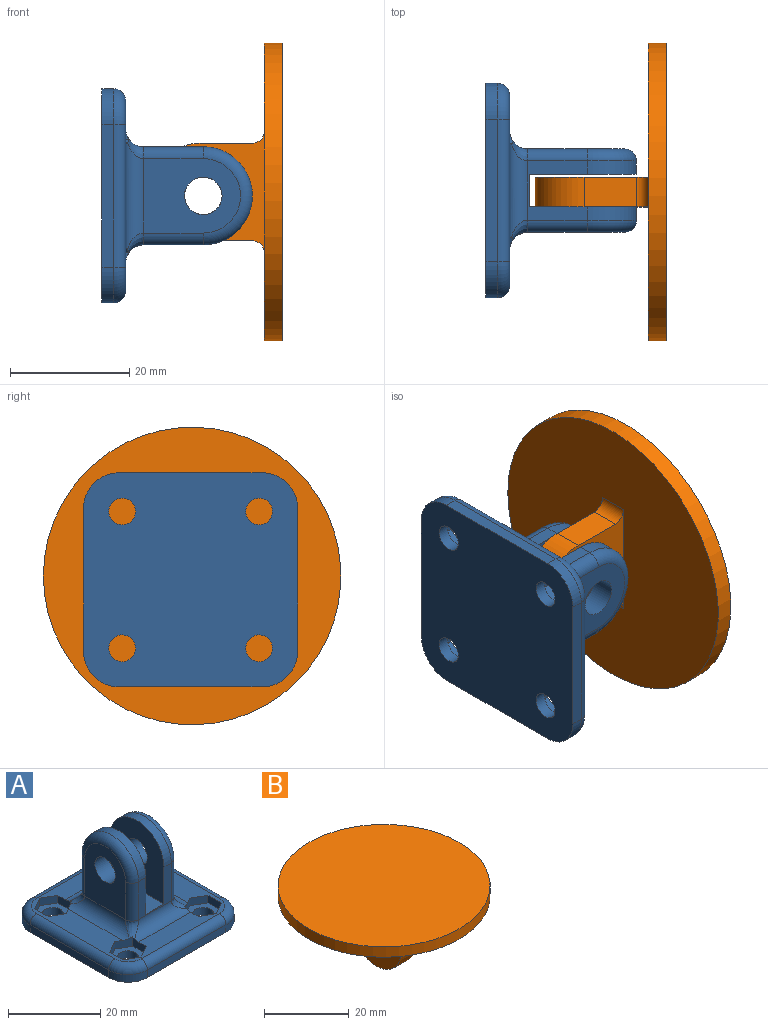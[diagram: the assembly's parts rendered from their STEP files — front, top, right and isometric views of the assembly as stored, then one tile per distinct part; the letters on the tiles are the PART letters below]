
ASSEMBLY  parts=2 mates=1
PART A: 75 faces, bbox 37x37x26 mm
  f0: plane 16.3x12.5mm, normal (1,0,0), area 155.8mm2, adj f51,f55,f71,f72,f73
  f1: plane 16.3x12.5mm, normal (-1,0,0), area 155.8mm2, adj f48,f53,f66,f67,f68
  f2: plane 18x16.5mm, normal (-1,0,0), area 236.6mm2, adj f4,f47,f52,f55,f56
  f3: plane 18x16.5mm, normal (1,0,0), area 236.6mm2, adj f4,f47,f52,f53,f54
  f4: plane 10.05x10mm, normal (0,-1,0), area 46.9mm2, adj f2,f3,f49,f52,f54,f56,f66,f71
  f5: plane 3.6x2.54mm, normal (0.5,0.87,0), area 8.7mm2, adj f6,f36,f37,f46,f51,f74
  f6: plane 4.15x2.54mm, normal (1,0,0), area 8.5mm2, adj f5,f7,f37,f46,f50,f74
  f7: plane 3.55x2.05mm, normal (0.5,-0.87,0), area 8.2mm2, adj f6,f8,f37,f46
  f8: plane 3.55x2.05mm, normal (-0.5,-0.87,0), area 8.2mm2, adj f7,f9,f37,f46
  f9: plane 4.1x2mm, normal (-1,0,0), area 8.2mm2, adj f8,f36,f37,f46
  f10: plane 3.55x2.05mm, normal (0.5,0.87,0), area 8.2mm2, adj f11,f32,f37,f42
  f11: plane 4.15x2.54mm, normal (1,0,0), area 8.5mm2, adj f10,f12,f37,f42,f49,f70
  f12: plane 3.6x2.54mm, normal (0.5,-0.87,0), area 8.7mm2, adj f11,f13,f37,f42,f51,f70
  f13: plane 3.55x2.05mm, normal (-0.5,-0.87,0), area 8.2mm2, adj f12,f14,f37,f42
  f14: plane 4.1x2mm, normal (-1,0,0), area 8.2mm2, adj f13,f32,f37,f42
  f15: plane 3.55x2.05mm, normal (-0.5,-0.87,0), area 8.2mm2, adj f16,f33,f37,f44
  f16: plane 4.15x2.54mm, normal (-1,0,0), area 8.5mm2, adj f15,f17,f37,f44,f50,f69
  f17: plane 3.6x2.54mm, normal (-0.5,0.87,0), area 8.7mm2, adj f16,f18,f37,f44,f48,f69
  f18: plane 3.55x2.05mm, normal (0.5,0.87,0), area 8.2mm2, adj f17,f19,f37,f44
  f19: plane 4.1x2mm, normal (1,0,0), area 8.2mm2, adj f18,f33,f37,f44
  f20: plane 3.6x2.54mm, normal (-0.5,-0.87,0), area 8.7mm2, adj f21,f34,f37,f40,f48,f65
  f21: plane 4.15x2.54mm, normal (-1,0,0), area 8.5mm2, adj f20,f22,f37,f40,f49,f65
  f22: plane 3.55x2.05mm, normal (-0.5,0.87,0), area 8.2mm2, adj f21,f23,f37,f40
  f23: plane 3.55x2.05mm, normal (0.5,0.87,0), area 8.2mm2, adj f22,f24,f37,f40
  f24: plane 4.1x2mm, normal (1,0,0), area 8.2mm2, adj f23,f34,f37,f40
  f25: plane 24x2mm, normal (0,-1,0), area 48mm2, adj f26,f35,f38,f61
  f26: cylinder r=6mm len=6mm, axis (0,0,-1), area 18.8mm2, adj f25,f27,f38,f59
  f27: plane 24x2mm, normal (1,0,0), area 48mm2, adj f26,f28,f38,f57
  f28: cylinder r=6mm len=6mm, axis (0,0,-1), area 18.8mm2, adj f27,f29,f38,f58
  f29: plane 24x2mm, normal (0,1,0), area 48mm2, adj f28,f30,f38,f60
  f30: cylinder r=6mm len=6mm, axis (0,0,-1), area 18.8mm2, adj f29,f31,f38,f62
  f31: plane 24x2mm, normal (-1,0,0), area 48mm2, adj f30,f35,f38,f64
  f32: plane 3.55x2.05mm, normal (-0.5,0.87,0), area 8.2mm2, adj f10,f14,f37,f42
  f33: plane 3.55x2.05mm, normal (0.5,-0.87,0), area 8.2mm2, adj f15,f19,f37,f44
  f34: plane 3.55x2.05mm, normal (0.5,-0.87,0), area 8.2mm2, adj f20,f24,f37,f40
  f35: cylinder r=6mm len=6mm, axis (0,0,-1), area 18.8mm2, adj f25,f31,f38,f63
  f36: plane 3.55x2.05mm, normal (-0.5,0.87,0), area 8.2mm2, adj f5,f9,f37,f46
  f37: plane 32x32mm, normal (0,0,1), area 405.2mm2, adj f5,f6,f7,f8,f9,f10,f11,f12
  f38: plane 36x36mm, normal (0,0,-1), area 1201.5mm2, adj f25,f26,f27,f28,f29,f30,f31,f35
  f39: cylinder r=2.25mm len=4.5mm, axis (0,0,-1), area 28.3mm2, adj f38,f40
  f40: plane 8.2x7.1mm, normal (0,0,1), area 27.8mm2, adj f20,f21,f22,f23,f24,f34,f39
  f41: cylinder r=2.25mm len=4.5mm, axis (0,0,-1), area 28.3mm2, adj f38,f42
  f42: plane 8.2x7.1mm, normal (0,0,1), area 27.8mm2, adj f10,f11,f12,f13,f14,f32,f41
  f43: cylinder r=2.25mm len=4.5mm, axis (0,0,-1), area 28.3mm2, adj f38,f44
  f44: plane 8.2x7.1mm, normal (0,0,1), area 27.8mm2, adj f15,f16,f17,f18,f19,f33,f43
  f45: cylinder r=2.25mm len=4.5mm, axis (0,0,-1), area 28.3mm2, adj f38,f46
  f46: plane 8.2x7.1mm, normal (0,0,1), area 27.8mm2, adj f5,f6,f7,f8,f9,f36,f45
  f47: plane 10.05x10mm, normal (0,1,0), area 46.9mm2, adj f2,f3,f50,f52,f54,f56,f68,f73
  f48: cylinder r=3mm len=18.07mm, axis (0,1,0), area 74.8mm2, adj f1,f17,f20,f37,f65,f69
  f49: cylinder r=3mm len=15.9mm, axis (-1,0,0), area 61.7mm2, adj f4,f11,f21,f37,f65,f70
  f50: cylinder r=3mm len=15.9mm, axis (1,0,0), area 61.7mm2, adj f6,f16,f37,f47,f69,f74
  f51: cylinder r=3mm len=18.07mm, axis (0,-1,0), area 74.8mm2, adj f0,f5,f12,f37,f70,f74
  f52: plane 16.5x5.5mm, normal (0,0,1), area 90.7mm2, adj f2,f3,f4,f47
  f53: cylinder r=3.15mm len=6.3mm, axis (1,0,0), area 84.1mm2, adj f1,f3
  f54: cylinder r=8.25mm len=16.5mm, axis (1,0,0), area 58.3mm2, adj f3,f4,f47,f67
  f55: cylinder r=3.15mm len=6.3mm, axis (1,0,0), area 84.1mm2, adj f0,f2
  f56: cylinder r=8.25mm len=16.5mm, axis (1,0,0), area 58.3mm2, adj f2,f4,f47,f72
  f57: cylinder r=2mm len=24mm, axis (0,-1,0), area 75.4mm2, adj f27,f37,f58,f59
  f58: torus R=4mm, axis (0,0,1), area 26mm2, adj f28,f37,f57,f60
  f59: torus R=4mm, axis (0,0,1), area 26mm2, adj f26,f37,f57,f61
  f60: cylinder r=2mm len=24mm, axis (1,0,0), area 75.4mm2, adj f29,f37,f58,f62
  f61: cylinder r=2mm len=24mm, axis (-1,0,0), area 75.4mm2, adj f25,f37,f59,f63
  f62: torus R=4mm, axis (0,0,1), area 26mm2, adj f30,f37,f60,f64
  f63: torus R=4mm, axis (0,0,1), area 26mm2, adj f35,f37,f61,f64
  f64: cylinder r=2mm len=24mm, axis (0,1,0), area 75.4mm2, adj f31,f37,f62,f63
  f65: bspline ~3.94x3.94mm, area 9.3mm2, adj f20,f21,f48,f49,f66
  f66: cylinder r=2mm len=10.05mm, axis (0,0,1), area 31.6mm2, adj f1,f4,f65,f67
  f67: torus R=6.25mm, axis (1,0,0), area 74.3mm2, adj f1,f54,f66,f68
  f68: cylinder r=2mm len=10.05mm, axis (0,0,-1), area 31.6mm2, adj f1,f47,f67,f69
  f69: bspline ~3.94x3.94mm, area 9.3mm2, adj f16,f17,f48,f50,f68
  f70: bspline ~3.94x3.94mm, area 9.3mm2, adj f11,f12,f49,f51,f71
  f71: cylinder r=2mm len=10.05mm, axis (0,0,-1), area 31.6mm2, adj f0,f4,f70,f72
  f72: torus R=6.25mm, axis (1,0,0), area 74.3mm2, adj f0,f56,f71,f73
  f73: cylinder r=2mm len=10.05mm, axis (0,0,1), area 31.6mm2, adj f0,f47,f72,f74
  f74: bspline ~3.94x3.94mm, area 9.3mm2, adj f5,f6,f50,f51,f73
PART B: 11 faces, bbox 50x50x22 mm
  f0: plane 50x50mm, normal (0,0,-1), area 1861.5mm2, adj f1,f3,f5,f9,f10
  f1: cylinder r=25mm len=50mm, axis (0,0,-1), area 471.2mm2, adj f0,f2
  f2: plane 50x50mm, normal (0,0,1), area 1963.5mm2, adj f1
  f3: plane 20.4x19mm, normal (1,0,0), area 251.3mm2, adj f0,f4,f6,f7,f8,f9,f10
  f4: plane 8.8x5mm, normal (0,1,0), area 44mm2, adj f3,f5,f7,f9
  f5: plane 20.4x19mm, normal (-1,0,0), area 251.3mm2, adj f0,f4,f6,f7,f8,f9,f10
  f6: plane 8.8x5mm, normal (0,-1,0), area 44mm2, adj f3,f5,f7,f10
  f7: cylinder r=8.2mm len=16.4mm, axis (1,0,0), area 128.8mm2, adj f3,f4,f5,f6
  f8: cylinder r=3.25mm len=6.5mm, axis (1,0,0), area 102.1mm2, adj f3,f5
  f9: cylinder r=2mm len=5mm, axis (-1,0,0), area 15.7mm2, adj f0,f3,f4,f5
  f10: cylinder r=2mm len=5mm, axis (1,0,0), area 15.7mm2, adj f0,f3,f5,f6
PLACE A rot(axis=(0.58,0.58,0.58),120deg) t=(-36,0.25,59.05)mm
PLACE B rot(axis=(0.58,0.58,0.58),120deg) t=(-8.7,0,59.7)mm
MATE fastened A.f53 <-> B.f8  axis (0,1,0) through (-18.95,-2.5,59.05)mm
